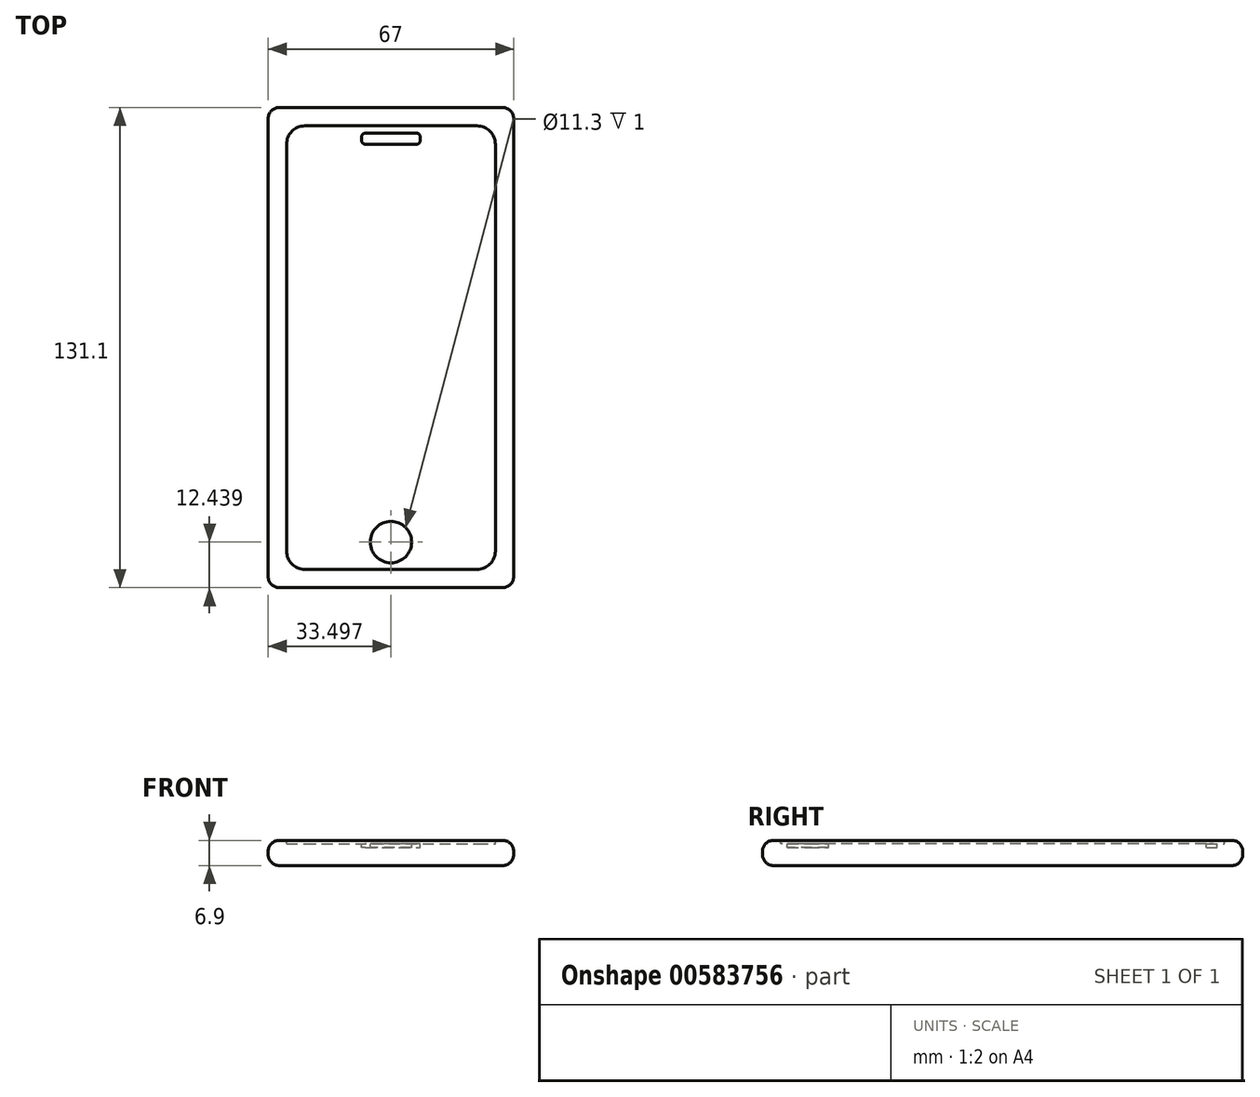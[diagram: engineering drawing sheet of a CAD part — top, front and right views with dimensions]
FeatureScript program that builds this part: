
annotation { "Feature Type Name" : "Feature", "Feature Type Description" : "" }
export const myFeature = defineFeature(function(context is Context, id is Id, definition is map)
    precondition{}
    {
        {
            var Q0;
            Q0=qCreatedBy(makeId("Top.planeOp"),FACE);
            var sketch = newSketch(context, id + "F0", { "sketchPlane" : qUnion([Q0])});
            skLineSegment(sketch, "E0.bottom", {"start": v(-53.13, 55.16) * mm, "end": v(13.87, 55.16) * mm});
            skLineSegment(sketch, "E0.top", {"start": v(-53.13, -75.94) * mm, "end": v(13.87, -75.94) * mm});
            skLineSegment(sketch, "E0.left", {"start": v(-53.13, 55.16) * mm, "end": v(-53.13, -75.94) * mm});
            skLineSegment(sketch, "E0.right", {"start": v(13.87, 55.16) * mm, "end": v(13.87, -75.94) * mm});
            skSolve(sketch);
        }
        {
            var Q0;
            Q0 = qSketchRegion(id + "F0", true);
            extrude(context, id + "F1", {"entities" : qUnion([Q0]), "depth" : 6.9 * mm, "offsetDistance" : 25 * mm});
        }
        {
            var Q0;
            Q0=makeQuery(id+"F1.opExtrude","CAP_FACE",FACE,{"disambiguationData":[OSD([sQuery(id+"F0.wireOp",EDGE,"E0.bottom"),sQuery(id+"F0.wireOp",EDGE,"E0.top"),sQuery(id+"F0.wireOp",EDGE,"E0.left"),sQuery(id+"F0.wireOp",EDGE,"E0.right")])],"isStart":false});
            var Q1;
            Q1=makeQuery(id+"F1.opExtrude","CAP_FACE",FACE,{"disambiguationData":[OSD([sQuery(id+"F0.wireOp",EDGE,"E0.bottom"),sQuery(id+"F0.wireOp",EDGE,"E0.top"),sQuery(id+"F0.wireOp",EDGE,"E0.left"),sQuery(id+"F0.wireOp",EDGE,"E0.right")])],"isStart":true});
            var Q2;
            Q2=makeQuery(id+"F1.opExtrude","CAP_EDGE",EDGE,{"disambiguationData":[OSD([sQuery(id+"F0.wireOp",EDGE,"E0.top")])],"isStart":true});
            var Q3;
            Q3=makeQuery(id+"F1.opExtrude","SWEPT_EDGE",EDGE,{"disambiguationData":[OSD([sQuery(id+"F0.wireOp",EDGE,"E0.top"),sQuery(id+"F0.wireOp",EDGE,"E0.right")])]});
            var Q4;
            Q4=makeQuery(id+"F1.opExtrude","SWEPT_EDGE",EDGE,{"disambiguationData":[OSD([sQuery(id+"F0.wireOp",EDGE,"E0.top"),sQuery(id+"F0.wireOp",EDGE,"E0.left")])]});
            var Q5;
            Q5=makeQuery(id+"F1.opExtrude","SWEPT_EDGE",EDGE,{"disambiguationData":[OSD([sQuery(id+"F0.wireOp",EDGE,"E0.bottom"),sQuery(id+"F0.wireOp",EDGE,"E0.right")])]});
            var Q6;
            Q6=makeQuery(id+"F1.opExtrude","SWEPT_EDGE",EDGE,{"disambiguationData":[OSD([sQuery(id+"F0.wireOp",EDGE,"E0.bottom"),sQuery(id+"F0.wireOp",EDGE,"E0.left")])]});
            fillet(context, id + "F2", {"entities" : qUnion([Q0, Q1, Q2, Q3, Q4, Q5, Q6]), "radius" : 3 * mm, "tangentPropagation" : true, "allowEdgeOverflow" : false});
        }
        {
            var Q0;
            Q0=makeQuery(id+"F1.opExtrude","CAP_FACE",FACE,{"disambiguationData":[OSD([sQuery(id+"F0.wireOp",EDGE,"E0.bottom"),sQuery(id+"F0.wireOp",EDGE,"E0.top"),sQuery(id+"F0.wireOp",EDGE,"E0.left"),sQuery(id+"F0.wireOp",EDGE,"E0.right")])],"isStart":false});
            var sketch = newSketch(context, id + "F3", { "sketchPlane" : qUnion([Q0])});
            skCircle(sketch, "E1", {"center": v(-19.63, -63.5) * mm, "radius": 5.65 * mm});
            skPoint(sketch, "E2.end.orphan", {"position": v(-19.63, -72.94) * mm});
            skPoint(sketch, "E3.orphan", {"position": v(-50.13, -72.94) * mm});
            skPoint(sketch, "E4.end.orphan", {"position": v(10.87, -72.94) * mm});
            skLineSegment(sketch, "E5", {"start": v(-19.63, 48.16) * mm, "end": v(-27.63, 48.16) * mm});
            skLineSegment(sketch, "E6.MirrorCS", {"start": v(-19.63, 48.16) * mm, "end": v(-11.63, 48.16) * mm});
            skLineSegment(sketch, "E7", {"start": v(-27.63, 48.16) * mm, "end": v(-27.63, 45.16) * mm});
            skLineSegment(sketch, "E8", {"start": v(-27.63, 45.16) * mm, "end": v(-11.63, 45.16) * mm});
            skLineSegment(sketch, "E9", {"start": v(-11.63, 45.16) * mm, "end": v(-11.63, 48.16) * mm});
            skPoint(sketch, "E10.start.orphan", {"position": v(-19.63, 52.16) * mm});
            skSolve(sketch);
        }
        {
            var Q0;
            Q0 = qSketchRegion(id + "F3", true);
            extrude(context, id + "F4", {"entities" : qUnion([Q0]), "operationType" : NewBodyOperationType.REMOVE, "oppositeDirection" : true, "depth" : 2 * mm, "offsetDistance" : 25 * mm});
        }
        {
            var Q0;
            Q0=makeQuery(id+"F4.boolean.opBoolean","COPY",EDGE,{"derivedFrom":makeQuery(id+"F4.opExtrude","SWEPT_EDGE",EDGE,{"disambiguationData":[OSD([sQuery(id+"F3.wireOp",EDGE,"E7"),sQuery(id+"F3.wireOp",EDGE,"E8")])]})});
            var Q1;
            Q1=makeQuery(id+"F4.boolean.opBoolean","COPY",EDGE,{"derivedFrom":makeQuery(id+"F4.opExtrude","SWEPT_EDGE",EDGE,{"disambiguationData":[OSD([sQuery(id+"F3.wireOp",EDGE,"E5"),sQuery(id+"F3.wireOp",EDGE,"E7")])]})});
            var Q2;
            Q2=makeQuery(id+"F4.boolean.opBoolean","COPY",EDGE,{"derivedFrom":makeQuery(id+"F4.opExtrude","SWEPT_EDGE",EDGE,{"disambiguationData":[OSD([sQuery(id+"F3.wireOp",EDGE,"E6.MirrorCS"),sQuery(id+"F3.wireOp",EDGE,"E9")])]})});
            var Q3;
            Q3=makeQuery(id+"F4.boolean.opBoolean","COPY",EDGE,{"derivedFrom":makeQuery(id+"F4.opExtrude","SWEPT_EDGE",EDGE,{"disambiguationData":[OSD([sQuery(id+"F3.wireOp",EDGE,"E8"),sQuery(id+"F3.wireOp",EDGE,"E9")])]})});
            fillet(context, id + "F5", {"entities" : qUnion([Q0, Q1, Q2, Q3]), "radius" : 1 * mm, "tangentPropagation" : true, "allowEdgeOverflow" : false});
        }
        {
            var Q0;
            Q0=makeQuery(id+"F1.opExtrude","CAP_FACE",FACE,{"disambiguationData":[OSD([sQuery(id+"F0.wireOp",EDGE,"E0.bottom"),sQuery(id+"F0.wireOp",EDGE,"E0.top"),sQuery(id+"F0.wireOp",EDGE,"E0.left"),sQuery(id+"F0.wireOp",EDGE,"E0.right")])],"isStart":false});
            var sketch = newSketch(context, id + "F6", { "sketchPlane" : qUnion([Q0])});
            skLineSegment(sketch, "E11", {"start": v(-50.13, 52.16) * mm, "end": v(-48.13, 52.16) * mm});
            skLineSegment(sketch, "E12", {"start": v(-48.13, 49.16) * mm, "end": v(-48.13, -70.94) * mm});
            skLineSegment(sketch, "E13", {"start": v(-48.13, -70.94) * mm, "end": v(8.87, -70.94) * mm});
            skLineSegment(sketch, "E14", {"start": v(8.87, -70.94) * mm, "end": v(8.87, 50.16) * mm});
            skPoint(sketch, "E15.orphan", {"position": v(10.87, -70.94) * mm});
            skPoint(sketch, "E16.orphan", {"position": v(-48.13, -72.94) * mm});
            skLineSegment(sketch, "E17", {"start": v(8.87, 50.16) * mm, "end": v(-48.13, 50.16) * mm});
            skLineSegment(sketch, "E18", {"start": v(-48.13, 50.16) * mm, "end": v(-48.13, 49.16) * mm});
            skPoint(sketch, "E19.start.orphan", {"position": v(8.87, 49.16) * mm});
            skPoint(sketch, "E20.orphan", {"position": v(8.87, 52.16) * mm});
            skSolve(sketch);
        }
        {
            var Q0;
            Q0 = qSketchRegion(id + "F6", true);
            extrude(context, id + "F7", {"entities" : qUnion([Q0]), "operationType" : NewBodyOperationType.REMOVE, "oppositeDirection" : true, "depth" : 1 * mm, "offsetDistance" : 25 * mm});
        }
        {
            var Q0;
            Q0=makeQuery(id+"F7.boolean.opBoolean","COPY",EDGE,{"derivedFrom":makeQuery(id+"F7.opExtrude","SWEPT_EDGE",EDGE,{"disambiguationData":[OSD([sQuery(id+"F6.wireOp",EDGE,"E17"),sQuery(id+"F6.wireOp",EDGE,"E18")])]})});
            var Q1;
            Q1=makeQuery(id+"F7.boolean.opBoolean","COPY",EDGE,{"derivedFrom":makeQuery(id+"F7.opExtrude","SWEPT_EDGE",EDGE,{"disambiguationData":[OSD([sQuery(id+"F6.wireOp",EDGE,"E14"),sQuery(id+"F6.wireOp",EDGE,"E17")])]})});
            var Q2;
            Q2=makeQuery(id+"F7.boolean.opBoolean","COPY",EDGE,{"derivedFrom":makeQuery(id+"F7.opExtrude","SWEPT_EDGE",EDGE,{"disambiguationData":[OSD([sQuery(id+"F6.wireOp",EDGE,"E13"),sQuery(id+"F6.wireOp",EDGE,"E14")])]})});
            var Q3;
            Q3=makeQuery(id+"F7.boolean.opBoolean","COPY",EDGE,{"derivedFrom":makeQuery(id+"F7.opExtrude","SWEPT_EDGE",EDGE,{"disambiguationData":[OSD([sQuery(id+"F6.wireOp",EDGE,"E12"),sQuery(id+"F6.wireOp",EDGE,"E13")])]})});
            fillet(context, id + "F8", {"entities" : qUnion([Q0, Q1, Q2, Q3]), "radius" : 5 * mm, "tangentPropagation" : true, "allowEdgeOverflow" : false});
        }
    });
